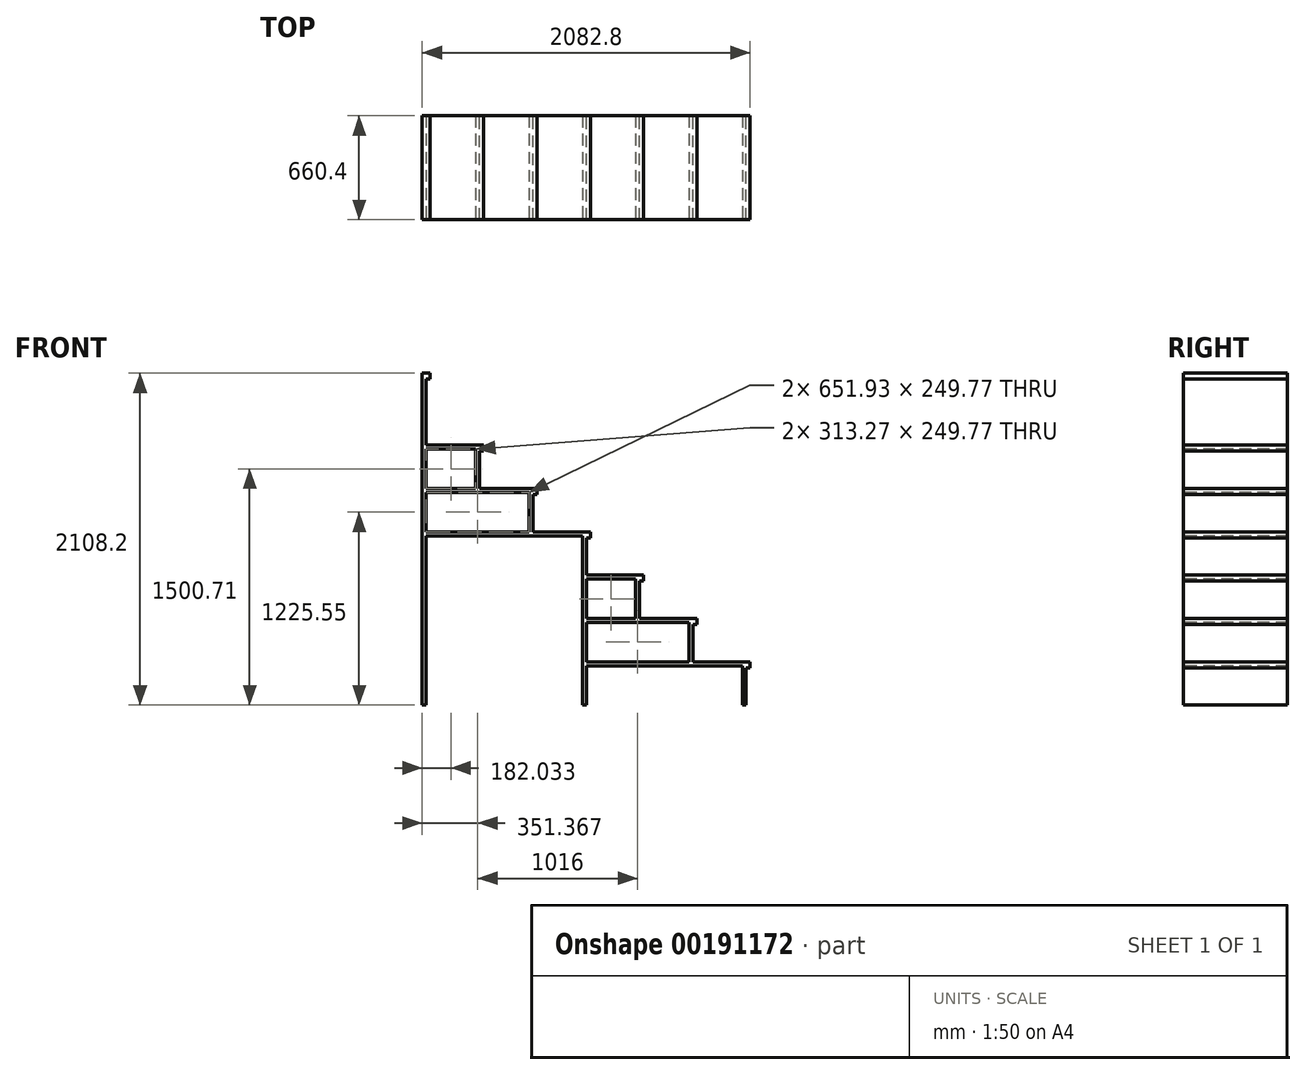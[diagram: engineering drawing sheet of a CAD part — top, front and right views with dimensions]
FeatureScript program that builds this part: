
annotation { "Feature Type Name" : "Feature", "Feature Type Description" : "" }
export const myFeature = defineFeature(function(context is Context, id is Id, definition is map)
    precondition{}
    {
        {
            var Q0;
            Q0=qCreatedBy(makeId("Front.planeOp"),FACE);
            var sketch = newSketch(context, id + "F0", { "sketchPlane" : qUnion([Q0])});
            skLineSegment(sketch, "E0", {"start": v(0, 1659.28) * mm, "end": v(0, -448.92) * mm});
            skLineSegment(sketch, "E1", {"start": v(0, -448.92) * mm, "end": v(2032, -448.92) * mm});
            skLineSegment(sketch, "E2", {"start": v(2032, -448.92) * mm, "end": v(2032, -173.76) * mm});
            skLineSegment(sketch, "E3", {"start": v(2032, -173.76) * mm, "end": v(1693.33, -173.76) * mm});
            skLineSegment(sketch, "E4", {"start": v(1693.33, -173.76) * mm, "end": v(1693.33, 101.41) * mm});
            skLineSegment(sketch, "E5", {"start": v(1693.33, 101.41) * mm, "end": v(1354.67, 101.41) * mm});
            skLineSegment(sketch, "E6", {"start": v(1354.67, 101.41) * mm, "end": v(1354.67, 376.58) * mm});
            skLineSegment(sketch, "E7", {"start": v(1354.67, 376.58) * mm, "end": v(1016, 376.58) * mm});
            skLineSegment(sketch, "E8", {"start": v(1016, 376.58) * mm, "end": v(1016, 651.74) * mm});
            skLineSegment(sketch, "E9", {"start": v(1016, 651.74) * mm, "end": v(677.33, 651.74) * mm});
            skLineSegment(sketch, "E10", {"start": v(677.33, 651.74) * mm, "end": v(677.33, 926.91) * mm});
            skLineSegment(sketch, "E11", {"start": v(677.33, 926.91) * mm, "end": v(338.67, 926.91) * mm});
            skLineSegment(sketch, "E12", {"start": v(338.67, 926.91) * mm, "end": v(338.67, 1202.08) * mm});
            skLineSegment(sketch, "E13", {"start": v(338.67, 1202.08) * mm, "end": v(0, 1202.08) * mm});
            skLineSegment(sketch, "E14", {"start": v(0, 1659.28) * mm, "end": v(-25.4, 1659.28) * mm});
            skLineSegment(sketch, "E15", {"start": v(-25.4, 1659.28) * mm, "end": v(-25.4, -448.92) * mm});
            skLineSegment(sketch, "E16", {"start": v(-25.4, -448.92) * mm, "end": v(0, -448.92) * mm});
            skSolve(sketch);
        }
        {
            var Q0;
            Q0 = qSketchRegion(id + "F0", true);
            extrude(context, id + "F1", {"entities" : qUnion([Q0]), "depth" : 660.4 * mm});
        }
        {
            var Q0;
            Q0=makeQuery(id+"F1.opExtrude","CAP_FACE",FACE,{"disambiguationData":[OSD([sQuery(id+"F0.wireOp",EDGE,"E0"),sQuery(id+"F0.wireOp",EDGE,"E1"),sQuery(id+"F0.wireOp",EDGE,"E2"),sQuery(id+"F0.wireOp",EDGE,"E3"),sQuery(id+"F0.wireOp",EDGE,"E4"),sQuery(id+"F0.wireOp",EDGE,"E5"),sQuery(id+"F0.wireOp",EDGE,"E6"),sQuery(id+"F0.wireOp",EDGE,"E7"),sQuery(id+"F0.wireOp",EDGE,"E8"),sQuery(id+"F0.wireOp",EDGE,"E9"),sQuery(id+"F0.wireOp",EDGE,"E10"),sQuery(id+"F0.wireOp",EDGE,"E11"),sQuery(id+"F0.wireOp",EDGE,"E12"),sQuery(id+"F0.wireOp",EDGE,"E13"),sQuery(id+"F0.wireOp",EDGE,"E14"),sQuery(id+"F0.wireOp",EDGE,"E15"),sQuery(id+"F0.wireOp",EDGE,"E16")])],"isStart":false});
            var sketch = newSketch(context, id + "F2", { "sketchPlane" : qUnion([Q0])});
            skLineSegment(sketch, "E17.bottom", {"start": v(0, 1176.68) * mm, "end": v(313.27, 1176.68) * mm});
            skLineSegment(sketch, "E17.top", {"start": v(0, 926.91) * mm, "end": v(313.27, 926.91) * mm});
            skLineSegment(sketch, "E17.left", {"start": v(0, 1176.68) * mm, "end": v(0, 926.91) * mm});
            skLineSegment(sketch, "E17.right", {"start": v(313.27, 1176.68) * mm, "end": v(313.27, 926.91) * mm});
            skLineSegment(sketch, "E18.bottom", {"start": v(0, 901.51) * mm, "end": v(651.93, 901.51) * mm});
            skLineSegment(sketch, "E18.top", {"start": v(0, 651.74) * mm, "end": v(651.93, 651.74) * mm});
            skLineSegment(sketch, "E18.left", {"start": v(0, 901.51) * mm, "end": v(0, 651.74) * mm});
            skLineSegment(sketch, "E18.right", {"start": v(651.93, 901.51) * mm, "end": v(651.93, 651.74) * mm});
            skLineSegment(sketch, "E19.bottom", {"start": v(0, 626.34) * mm, "end": v(990.6, 626.34) * mm});
            skLineSegment(sketch, "E19.top", {"start": v(0, -448.92) * mm, "end": v(990.6, -448.92) * mm});
            skLineSegment(sketch, "E19.left", {"start": v(0, 626.34) * mm, "end": v(0, -448.92) * mm});
            skLineSegment(sketch, "E19.right", {"start": v(990.6, 626.34) * mm, "end": v(990.6, -448.92) * mm});
            skLineSegment(sketch, "E20.bottom", {"start": v(1016, 351.18) * mm, "end": v(1329.27, 351.18) * mm});
            skLineSegment(sketch, "E20.top", {"start": v(1016, 101.41) * mm, "end": v(1329.27, 101.41) * mm});
            skLineSegment(sketch, "E20.left", {"start": v(1016, 351.18) * mm, "end": v(1016, 101.41) * mm});
            skLineSegment(sketch, "E20.right", {"start": v(1329.27, 351.18) * mm, "end": v(1329.27, 101.41) * mm});
            skLineSegment(sketch, "E21.bottom", {"start": v(1016, 76.01) * mm, "end": v(1667.93, 76.01) * mm});
            skLineSegment(sketch, "E21.top", {"start": v(1016, -173.76) * mm, "end": v(1667.93, -173.76) * mm});
            skLineSegment(sketch, "E21.left", {"start": v(1016, 76.01) * mm, "end": v(1016, -173.76) * mm});
            skLineSegment(sketch, "E21.right", {"start": v(1667.93, 76.01) * mm, "end": v(1667.93, -173.76) * mm});
            skLineSegment(sketch, "E22.bottom", {"start": v(1016, -199.16) * mm, "end": v(2006.6, -199.16) * mm});
            skLineSegment(sketch, "E22.top", {"start": v(1016, -448.92) * mm, "end": v(2006.6, -448.92) * mm});
            skLineSegment(sketch, "E22.left", {"start": v(1016, -199.16) * mm, "end": v(1016, -448.92) * mm});
            skLineSegment(sketch, "E22.right", {"start": v(2006.6, -199.16) * mm, "end": v(2006.6, -448.92) * mm});
            skSolve(sketch);
        }
        {
            var Q0;
            Q0 = qSketchRegion(id + "F2", true);
            extrude(context, id + "F3", {"entities" : qUnion([Q0]), "operationType" : NewBodyOperationType.REMOVE, "oppositeDirection" : true, "depth" : 660.4 * mm});
        }
        {
            var Q0;
            Q0=makeQuery(id+"F1.opExtrude","SWEPT_FACE",FACE,{"disambiguationData":[OSD([sQuery(id+"F0.wireOp",EDGE,"E0")])]});
            var sketch = newSketch(context, id + "F4", { "sketchPlane" : qUnion([Q0])});
            skLineSegment(sketch, "E23.bottom", {"start": v(-660.4, 1659.28) * mm, "end": v(0, 1659.28) * mm});
            skLineSegment(sketch, "E23.top", {"start": v(-660.4, 1621.18) * mm, "end": v(0, 1621.18) * mm});
            skLineSegment(sketch, "E23.left", {"start": v(-660.4, 1659.28) * mm, "end": v(-660.4, 1621.18) * mm});
            skLineSegment(sketch, "E23.right", {"start": v(0, 1659.28) * mm, "end": v(0, 1621.18) * mm});
            skSolve(sketch);
        }
        {
            var Q0;
            Q0 = qSketchRegion(id + "F4", true);
            extrude(context, id + "F5", {"entities" : qUnion([Q0]), "operationType" : NewBodyOperationType.ADD, "depth" : 25.4 * mm});
        }
        {
            var Q0;
            Q0=makeQuery(id+"F1.opExtrude","SWEPT_FACE",FACE,{"disambiguationData":[OSD([sQuery(id+"F0.wireOp",EDGE,"E12")])]});
            var sketch = newSketch(context, id + "F6", { "sketchPlane" : qUnion([Q0])});
            skLineSegment(sketch, "E24.bottom", {"start": v(-660.4, 1202.08) * mm, "end": v(0, 1202.08) * mm});
            skLineSegment(sketch, "E24.top", {"start": v(-660.4, 1163.98) * mm, "end": v(0, 1163.98) * mm});
            skLineSegment(sketch, "E24.left", {"start": v(-660.4, 1202.08) * mm, "end": v(-660.4, 1163.98) * mm});
            skLineSegment(sketch, "E24.right", {"start": v(0, 1202.08) * mm, "end": v(0, 1163.98) * mm});
            skSolve(sketch);
        }
        {
            var Q0;
            Q0 = qSketchRegion(id + "F6", true);
            extrude(context, id + "F7", {"entities" : qUnion([Q0]), "operationType" : NewBodyOperationType.ADD, "depth" : 25.4 * mm});
        }
        {
            var Q0;
            Q0=makeQuery(id+"F1.opExtrude","SWEPT_FACE",FACE,{"disambiguationData":[OSD([sQuery(id+"F0.wireOp",EDGE,"E10")])]});
            var sketch = newSketch(context, id + "F8", { "sketchPlane" : qUnion([Q0])});
            skLineSegment(sketch, "E25.bottom", {"start": v(-660.4, 926.91) * mm, "end": v(0, 926.91) * mm});
            skLineSegment(sketch, "E25.top", {"start": v(-660.4, 888.81) * mm, "end": v(0, 888.81) * mm});
            skLineSegment(sketch, "E25.left", {"start": v(-660.4, 926.91) * mm, "end": v(-660.4, 888.81) * mm});
            skLineSegment(sketch, "E25.right", {"start": v(0, 926.91) * mm, "end": v(0, 888.81) * mm});
            skSolve(sketch);
        }
        {
            var Q0;
            Q0 = qSketchRegion(id + "F8", true);
            extrude(context, id + "F9", {"entities" : qUnion([Q0]), "operationType" : NewBodyOperationType.ADD, "depth" : 25.4 * mm});
        }
        {
            var Q0;
            Q0=makeQuery(id+"F1.opExtrude","SWEPT_FACE",FACE,{"disambiguationData":[OSD([sQuery(id+"F0.wireOp",EDGE,"E8")])]});
            var sketch = newSketch(context, id + "F10", { "sketchPlane" : qUnion([Q0])});
            skLineSegment(sketch, "E26.bottom", {"start": v(-660.4, 651.74) * mm, "end": v(0, 651.74) * mm});
            skLineSegment(sketch, "E26.top", {"start": v(-660.4, 613.64) * mm, "end": v(0, 613.64) * mm});
            skLineSegment(sketch, "E26.left", {"start": v(-660.4, 651.74) * mm, "end": v(-660.4, 613.64) * mm});
            skLineSegment(sketch, "E26.right", {"start": v(0, 651.74) * mm, "end": v(0, 613.64) * mm});
            skSolve(sketch);
        }
        {
            var Q0;
            Q0 = qSketchRegion(id + "F10", true);
            extrude(context, id + "F11", {"entities" : qUnion([Q0]), "operationType" : NewBodyOperationType.ADD, "depth" : 25.4 * mm});
        }
        {
            var Q0;
            Q0=makeQuery(id+"F1.opExtrude","SWEPT_FACE",FACE,{"disambiguationData":[OSD([sQuery(id+"F0.wireOp",EDGE,"E6")])]});
            var sketch = newSketch(context, id + "F12", { "sketchPlane" : qUnion([Q0])});
            skLineSegment(sketch, "E27.bottom", {"start": v(0, 376.58) * mm, "end": v(-660.4, 376.58) * mm});
            skLineSegment(sketch, "E27.top", {"start": v(0, 338.48) * mm, "end": v(-660.4, 338.48) * mm});
            skLineSegment(sketch, "E27.left", {"start": v(0, 376.58) * mm, "end": v(0, 338.48) * mm});
            skLineSegment(sketch, "E27.right", {"start": v(-660.4, 376.58) * mm, "end": v(-660.4, 338.48) * mm});
            skSolve(sketch);
        }
        {
            var Q0;
            Q0 = qSketchRegion(id + "F12", true);
            extrude(context, id + "F13", {"entities" : qUnion([Q0]), "operationType" : NewBodyOperationType.ADD, "depth" : 25.4 * mm});
        }
        {
            var Q0;
            Q0=makeQuery(id+"F1.opExtrude","SWEPT_FACE",FACE,{"disambiguationData":[OSD([sQuery(id+"F0.wireOp",EDGE,"E4")])]});
            var sketch = newSketch(context, id + "F14", { "sketchPlane" : qUnion([Q0])});
            skLineSegment(sketch, "E28.bottom", {"start": v(-660.4, 101.41) * mm, "end": v(0, 101.41) * mm});
            skLineSegment(sketch, "E28.top", {"start": v(-660.4, 63.31) * mm, "end": v(0, 63.31) * mm});
            skLineSegment(sketch, "E28.left", {"start": v(-660.4, 101.41) * mm, "end": v(-660.4, 63.31) * mm});
            skLineSegment(sketch, "E28.right", {"start": v(0, 101.41) * mm, "end": v(0, 63.31) * mm});
            skSolve(sketch);
        }
        {
            var Q0;
            Q0 = qSketchRegion(id + "F14", true);
            extrude(context, id + "F15", {"entities" : qUnion([Q0]), "operationType" : NewBodyOperationType.ADD, "depth" : 25.4 * mm});
        }
        {
            var Q0;
            Q0=makeQuery(id+"F1.opExtrude","SWEPT_FACE",FACE,{"disambiguationData":[OSD([sQuery(id+"F0.wireOp",EDGE,"E2")])]});
            var sketch = newSketch(context, id + "F16", { "sketchPlane" : qUnion([Q0])});
            skLineSegment(sketch, "E29.bottom", {"start": v(-660.4, -173.76) * mm, "end": v(0, -173.76) * mm});
            skLineSegment(sketch, "E29.top", {"start": v(-660.4, -211.86) * mm, "end": v(0, -211.86) * mm});
            skLineSegment(sketch, "E29.left", {"start": v(-660.4, -173.76) * mm, "end": v(-660.4, -211.86) * mm});
            skLineSegment(sketch, "E29.right", {"start": v(0, -173.76) * mm, "end": v(0, -211.86) * mm});
            skSolve(sketch);
        }
        {
            var Q0;
            Q0 = qSketchRegion(id + "F16", true);
            extrude(context, id + "F17", {"entities" : qUnion([Q0]), "operationType" : NewBodyOperationType.ADD, "depth" : 25.4 * mm});
        }
    });
